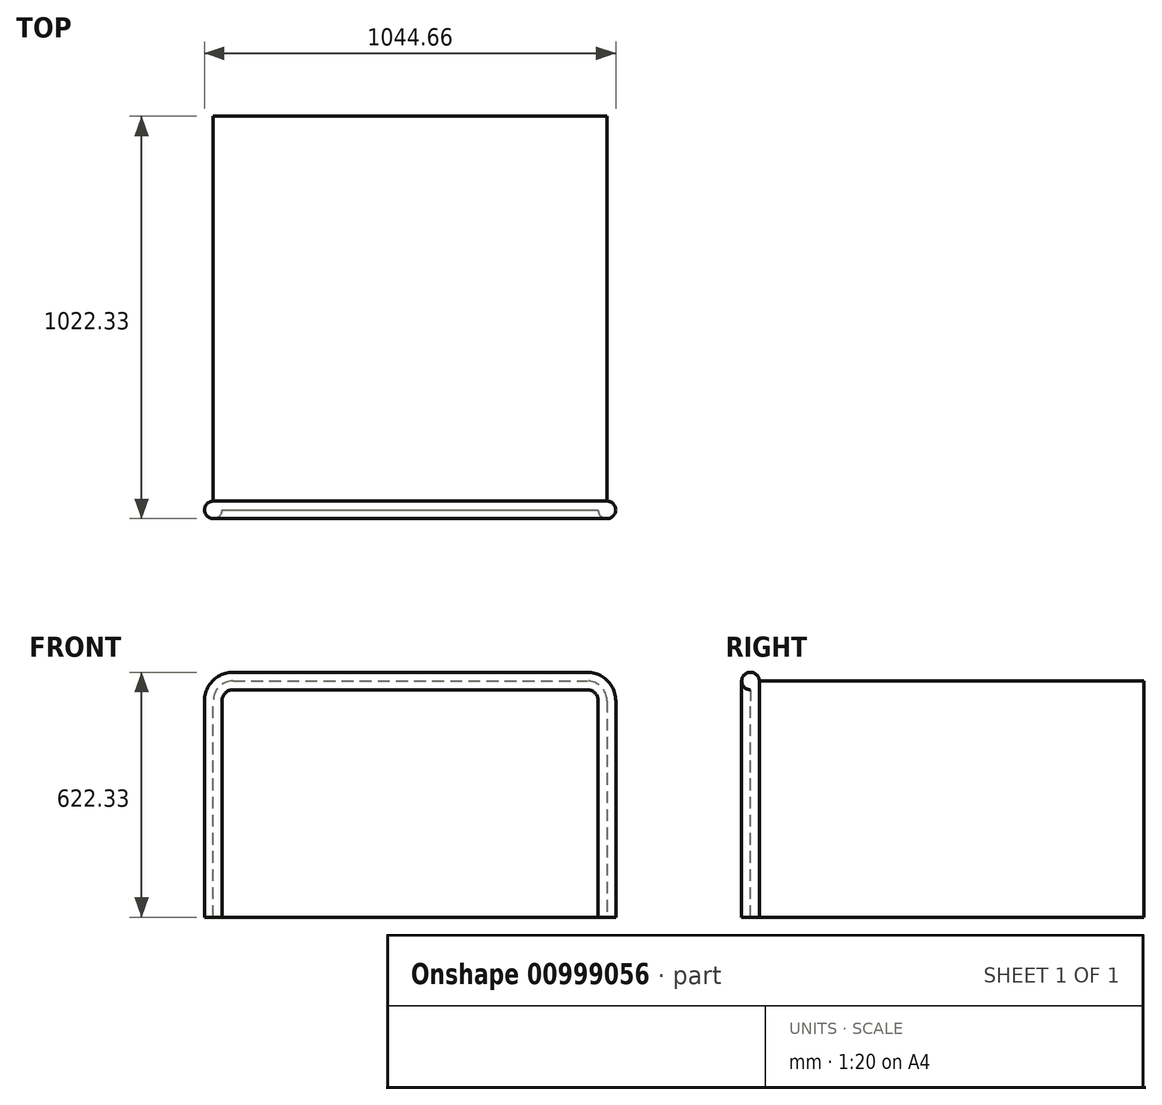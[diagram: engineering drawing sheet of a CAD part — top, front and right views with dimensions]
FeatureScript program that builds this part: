
annotation { "Feature Type Name" : "Feature", "Feature Type Description" : "" }
export const myFeature = defineFeature(function(context is Context, id is Id, definition is map)
    precondition{}
    {
        {
            var Q0;
            Q0=qCreatedBy(makeId("Front.planeOp"),FACE);
            var sketch = newSketch(context, id + "F0", { "sketchPlane" : qUnion([Q0])});
            skLineSegment(sketch, "E0.bottom", {"start": v(-433.2, -399.23) * mm, "end": v(566.8, -399.23) * mm});
            skLineSegment(sketch, "E0.top", {"start": v(-433.2, 200.77) * mm, "end": v(566.8, 200.77) * mm});
            skLineSegment(sketch, "E0.left", {"start": v(-433.2, -399.23) * mm, "end": v(-433.2, 200.77) * mm});
            skLineSegment(sketch, "E0.right", {"start": v(566.8, -399.23) * mm, "end": v(566.8, 200.77) * mm});
            skSolve(sketch);
        }
        {
            var Q0;
            Q0=makeQuery(id+"F0.imprint","IMPRINT",FACE,{"disambiguationData":[TD([[makeQuery(id+"F0.imprint","IMPRINT",EDGE,{"derivedFrom":sQuery(id+"F0.wireOp",EDGE,"E0.bottom")}),1.0]])]});
            extrude(context, id + "F1", {"entities" : qUnion([Q0]), "depth" : 1000 * mm, "offsetDistance" : 25 * mm});
        }
        {
            var Q0;
            Q0=makeQuery(id+"F1.opExtrude","SWEPT_EDGE",EDGE,{"disambiguationData":[OSD([sQuery(id+"F0.wireOp",EDGE,"E0.top"),sQuery(id+"F0.wireOp",EDGE,"E0.left")])]});
            fillet(context, id + "F2", {"entities" : qUnion([Q0]), "radius" : 50 * mm, "tangentPropagation" : true, "allowEdgeOverflow" : false});
        }
        {
            var Q0;
            Q0=makeQuery(id+"F1.opExtrude","SWEPT_EDGE",EDGE,{"disambiguationData":[OSD([sQuery(id+"F0.wireOp",EDGE,"E0.top"),sQuery(id+"F0.wireOp",EDGE,"E0.right")])]});
            fillet(context, id + "F3", {"entities" : qUnion([Q0]), "radius" : 50 * mm, "tangentPropagation" : true, "allowEdgeOverflow" : false});
        }
        {
            var Q0;
            Q0=makeQuery(id+"F1.opExtrude","SWEPT_FACE",FACE,{"disambiguationData":[OSD([sQuery(id+"F0.wireOp",EDGE,"E0.bottom")])]});
            var sketch = newSketch(context, id + "F4", { "sketchPlane" : qUnion([Q0])});
            skCircle(sketch, "E1", {"center": v(-433.2, 1000) * mm, "radius": 22.33 * mm});
            skSolve(sketch);
        }
        {
            var Q0;
            {var subQ0=sQuery(id+"F4.wireOp",EDGE,"E1");var subQ1=sQuery(id+"F0.wireOp",EDGE,"E0.bottom");var subQ4=makeQuery(id+"F1.opExtrude","CAP_EDGE",EDGE,{"disambiguationData":[OSD([subQ1])],"isStart":false});var subQ5=makeQuery(id+"F4.imprint","INTERSECT",VERTEX,{"derivedFrom":[subQ4,subQ0]});Q0=makeQuery(id+"F4.imprint","IMPRINT",FACE,{"disambiguationData":[TD([[makeQuery(id+"F4.imprint","IMPRINT",EDGE,{"disambiguationData":[TD([[subQ5,1.0]])],"derivedFrom":subQ0}),1.0]])]});}
            var Q1;
            {var subQ0=sQuery(id+"F4.wireOp",EDGE,"E1");var subQ1=sQuery(id+"F0.wireOp",EDGE,"E0.bottom");var subQ4=makeQuery(id+"F1.opExtrude","CAP_EDGE",EDGE,{"disambiguationData":[OSD([subQ1])],"isStart":false});var subQ5=makeQuery(id+"F4.imprint","INTERSECT",VERTEX,{"derivedFrom":[subQ4,subQ0]});Q1=makeQuery(id+"F4.imprint","IMPRINT",FACE,{"disambiguationData":[TD([[makeQuery(id+"F4.imprint","IMPRINT",EDGE,{"disambiguationData":[TD([[subQ5,-1.0]])],"derivedFrom":subQ0}),1.0]])]});}
            var Q2;
            Q2=makeQuery(id+"F1.opExtrude","CAP_EDGE",EDGE,{"disambiguationData":[OSD([sQuery(id+"F0.wireOp",EDGE,"E0.left")])],"isStart":false});
            var Q3;
            {var subQ0=sQuery(id+"F0.wireOp",EDGE,"E0.left");var subQ1=sQuery(id+"F0.wireOp",EDGE,"E0.top");Q3=makeQuery(id+"F2.opFillet","BLEND_EDGE",EDGE,{"blendedFrom":[makeQuery(id+"F1.opExtrude","SWEPT_EDGE",EDGE,{"disambiguationData":[OSD([subQ1,subQ0])]}),makeQuery(id+"F1.opExtrude","CAP_FACE",FACE,{"disambiguationData":[OSD([sQuery(id+"F0.wireOp",EDGE,"E0.bottom"),subQ1,subQ0,sQuery(id+"F0.wireOp",EDGE,"E0.right")])],"isStart":false})],"blendedInto":[makeQuery(id+"F1.opExtrude","CAP_FACE",FACE,{"disambiguationData":[OSD([sQuery(id+"F0.wireOp",EDGE,"E0.bottom"),subQ1,subQ0,sQuery(id+"F0.wireOp",EDGE,"E0.right")])],"isStart":false})]});}
            var Q4;
            Q4=makeQuery(id+"F1.opExtrude","CAP_EDGE",EDGE,{"disambiguationData":[OSD([sQuery(id+"F0.wireOp",EDGE,"E0.top")])],"isStart":false});
            var Q5;
            {var subQ0=sQuery(id+"F0.wireOp",EDGE,"E0.right");var subQ1=sQuery(id+"F0.wireOp",EDGE,"E0.top");Q5=makeQuery(id+"F3.opFillet","BLEND_EDGE",EDGE,{"blendedFrom":[makeQuery(id+"F1.opExtrude","SWEPT_EDGE",EDGE,{"disambiguationData":[OSD([subQ1,subQ0])]}),makeQuery(id+"F1.opExtrude","CAP_FACE",FACE,{"disambiguationData":[OSD([sQuery(id+"F0.wireOp",EDGE,"E0.bottom"),subQ1,sQuery(id+"F0.wireOp",EDGE,"E0.left"),subQ0])],"isStart":false})],"blendedInto":[makeQuery(id+"F1.opExtrude","CAP_FACE",FACE,{"disambiguationData":[OSD([sQuery(id+"F0.wireOp",EDGE,"E0.bottom"),subQ1,sQuery(id+"F0.wireOp",EDGE,"E0.left"),subQ0])],"isStart":false})]});}
            var Q6;
            Q6=makeQuery(id+"F1.opExtrude","CAP_EDGE",EDGE,{"disambiguationData":[OSD([sQuery(id+"F0.wireOp",EDGE,"E0.right")])],"isStart":false});
            sweep(context, id + "F5", {"operationType" : NewBodyOperationType.ADD, "profiles" : qUnion([Q0, Q1]), "path" : qUnion([Q2, Q3, Q4, Q5, Q6])});
        }
    });
